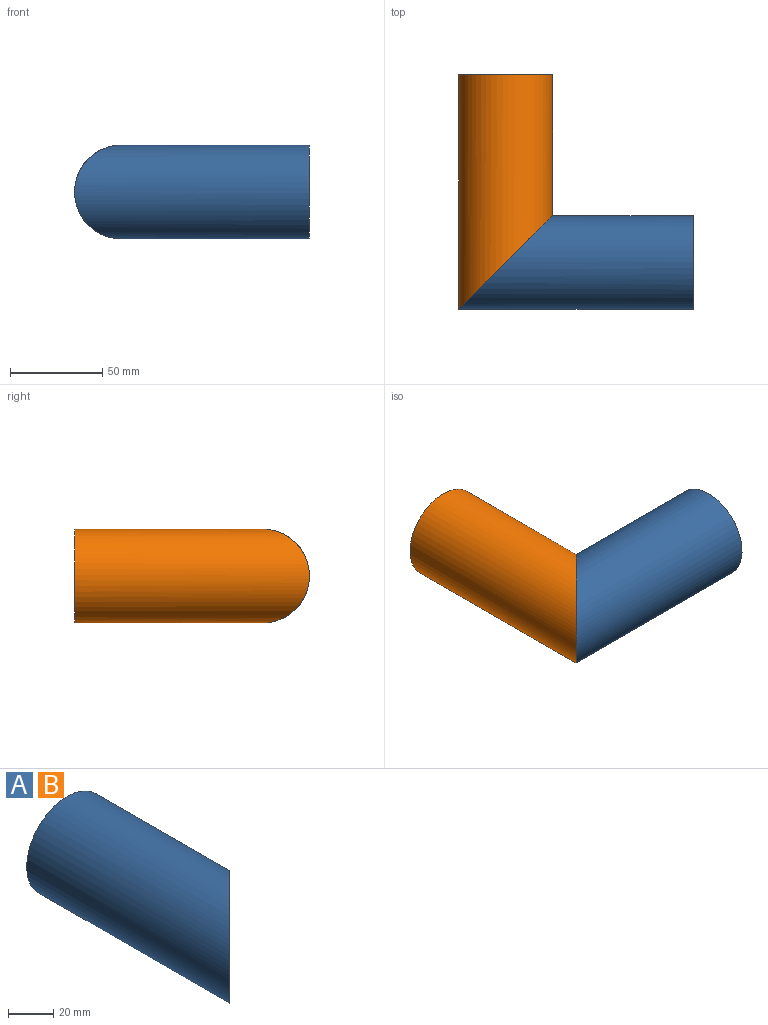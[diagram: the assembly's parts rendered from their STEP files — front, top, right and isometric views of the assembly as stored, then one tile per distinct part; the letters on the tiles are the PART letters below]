
ASSEMBLY  parts=2 mates=1
PART A: 4 faces, bbox 61.5x137.7x61.5 mm
  f0: cylinder r=19.05mm len=120.65mm, axis (0,-1,0), area 12083.1mm2, adj f2,f3
  f1: cylinder r=25.4mm len=127mm, axis (0,-1,0), area 16076.2mm2, adj f2,f3
  f2: plane 50.8x50.8mm, normal (0,1,0), area 886.7mm2, adj f0,f1
  f3: plane 61.48x61.48mm, normal (0.71,-0.71,0), area 1254mm2, adj f0,f1
PART B: same geometry as A
PLACE A rot(axis=(0.71,0.71,0),180deg) t=(-85.39,25.19,3.98)mm
PLACE B t=(-59.99,-0.21,3.98)mm
MATE fastened A.f3 <-> B.f3  axis (-0.71,0.71,0) through (-59.99,25.19,3.98)mm
